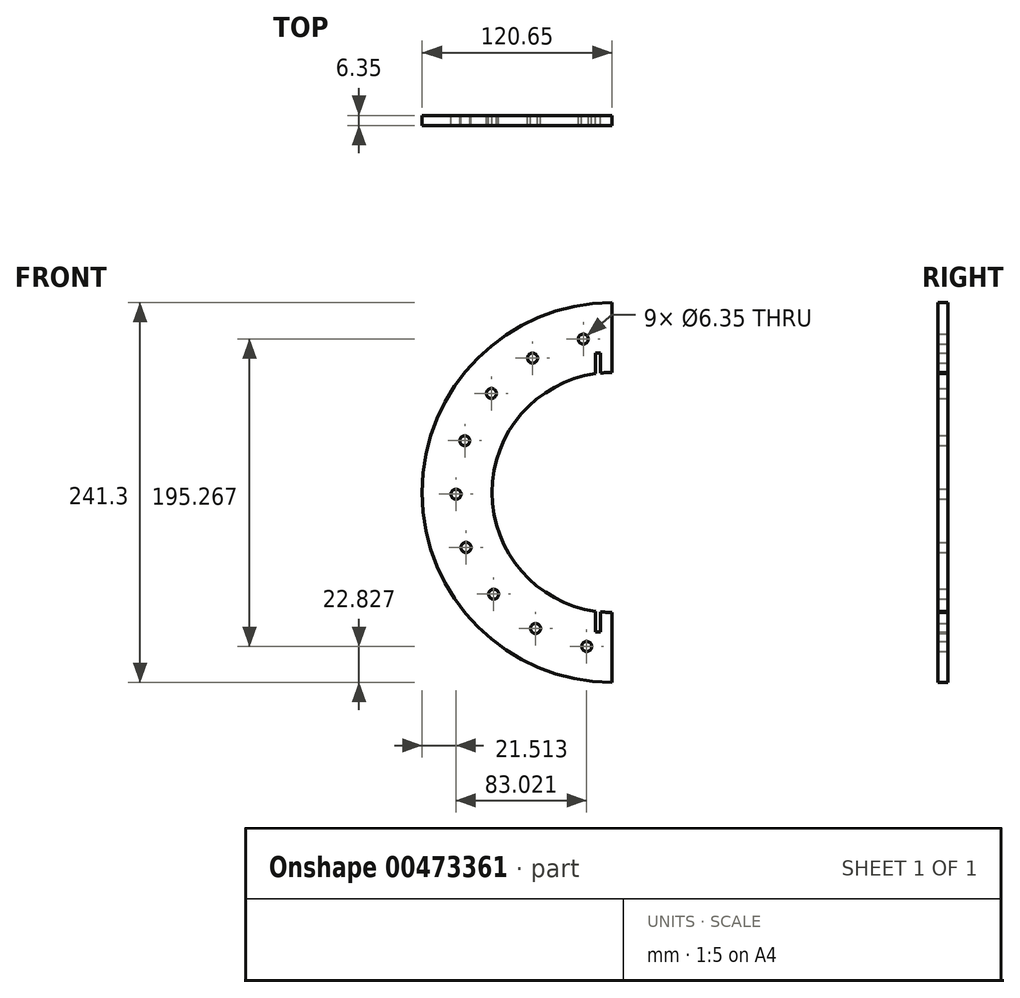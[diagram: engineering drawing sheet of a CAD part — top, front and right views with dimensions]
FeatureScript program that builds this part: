
annotation { "Feature Type Name" : "Feature", "Feature Type Description" : "" }
export const myFeature = defineFeature(function(context is Context, id is Id, definition is map)
    precondition{}
    {
        {
            var Q0;
            Q0=qCreatedBy(makeId("Front.planeOp"),FACE);
            var sketch = newSketch(context, id + "F0", { "sketchPlane" : qUnion([Q0])});
            skArc(sketch, "E0", {"start": v(-44.84, 143.8) * mm, "mid": v(-165.49, 23.15) * mm, "end": v(-44.84, -97.5) * mm});
            skArc(sketch, "E1", {"start": v(-55.38, 98.62) * mm, "mid": v(-121.04, 23.15) * mm, "end": v(-55.38, -52.31) * mm});
            skLineSegment(sketch, "E2", {"start": v(-44.84, 99.35) * mm, "end": v(-44.84, 143.8) * mm});
            skLineSegment(sketch, "E3", {"start": v(-44.84, 143.8) * mm, "end": v(-44.84, 99.35) * mm});
            skCircle(sketch, "E4", {"center": v(-60.96, -74.67) * mm, "radius": 3.18 * mm});
            skLineSegment(sketch, "E5", {"start": v(-55.38, 111.7) * mm, "end": v(-52.2, 111.7) * mm});
            skLineSegment(sketch, "E6", {"start": v(-52.2, 111.7) * mm, "end": v(-52.2, 99) * mm});
            skLineSegment(sketch, "E7", {"start": v(-52.2, -52.69) * mm, "end": v(-52.2, -65.39) * mm});
            skLineSegment(sketch, "E8", {"start": v(-52.2, -65.39) * mm, "end": v(-55.38, -65.39) * mm});
            skLineSegment(sketch, "E9", {"start": v(-55.38, -65.39) * mm, "end": v(-55.38, -52.31) * mm});
            skLineSegment(sketch, "E10", {"start": v(-55.38, 111.7) * mm, "end": v(-55.38, 98.62) * mm});
            skArc(sketch, "E11.trimOffspring", {"start": v(-52.2, -52.69) * mm, "mid": v(-48.52, -52.96) * mm, "end": v(-44.84, -53.05) * mm});
            skArc(sketch, "E12.trimOffspring", {"start": v(-44.84, 99.35) * mm, "mid": v(-48.52, 99.26) * mm, "end": v(-52.2, 99) * mm});
            skLineSegment(sketch, "E13.trimOffspring", {"start": v(-44.84, -53.05) * mm, "end": v(-44.84, -97.5) * mm});
            skCircle(sketch, "E14.2.10.0", {"center": v(-63.15, 120.6) * mm, "radius": 3.18 * mm});
            skCircle(sketch, "E14.2.11.0", {"center": v(-95.37, 108.45) * mm, "radius": 3.18 * mm});
            skCircle(sketch, "E14.2.12.0", {"center": v(-121.5, 86.03) * mm, "radius": 3.18 * mm});
            skCircle(sketch, "E14.2.13.0", {"center": v(-138.38, 56.02) * mm, "radius": 3.17 * mm});
            skCircle(sketch, "E14.2.14.0", {"center": v(-143.98, 22.04) * mm, "radius": 3.18 * mm});
            skCircle(sketch, "E15.2.15.0", {"center": v(-137.62, -11.8) * mm, "radius": 3.18 * mm});
            skCircle(sketch, "E15.2.16.0", {"center": v(-120.07, -41.42) * mm, "radius": 3.18 * mm});
            skCircle(sketch, "E15.2.17.0", {"center": v(-93.44, -63.26) * mm, "radius": 3.18 * mm});
            skSolve(sketch);
        }
        {
            var Q0;
            Q0=makeQuery(id+"F0.imprint","IMPRINT",FACE,{"disambiguationData":[TD([[makeQuery(id+"F0.imprint","IMPRINT",EDGE,{"derivedFrom":sQuery(id+"F0.wireOp",EDGE,"E0")}),1.0]])]});
            extrude(context, id + "F1", {"entities" : qUnion([Q0]), "depth" : 6.35 * mm});
        }
    });
